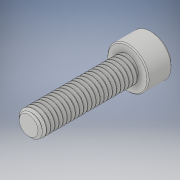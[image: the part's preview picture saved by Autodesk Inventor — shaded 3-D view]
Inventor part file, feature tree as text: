
AUTODESK INVENTOR PART (.ipt)
format: ipt  version: 2018 (Build 220112000, 112)  size: 892,928 bytes
history: native  units: in
note: dims shown in document units (in); Inventor stores cm internally (conversion verified against a paired STEP export)
features: chamfer x1
ambient origin geometry x8: Origin, YZ Plane, XZ Plane, XY Plane, X Axis, Y Axis, Z Axis, Center Point
bodies: Solid1 (feature_tree)
feature tree (1):
  chamfer  "Chamfer2"  [1 undecoded]
note: 1 required parameter value undecoded (feature->parameter linkage not recoverable at this tier; creation-order binding heuristic only, values carry confidence <= 0.55)
